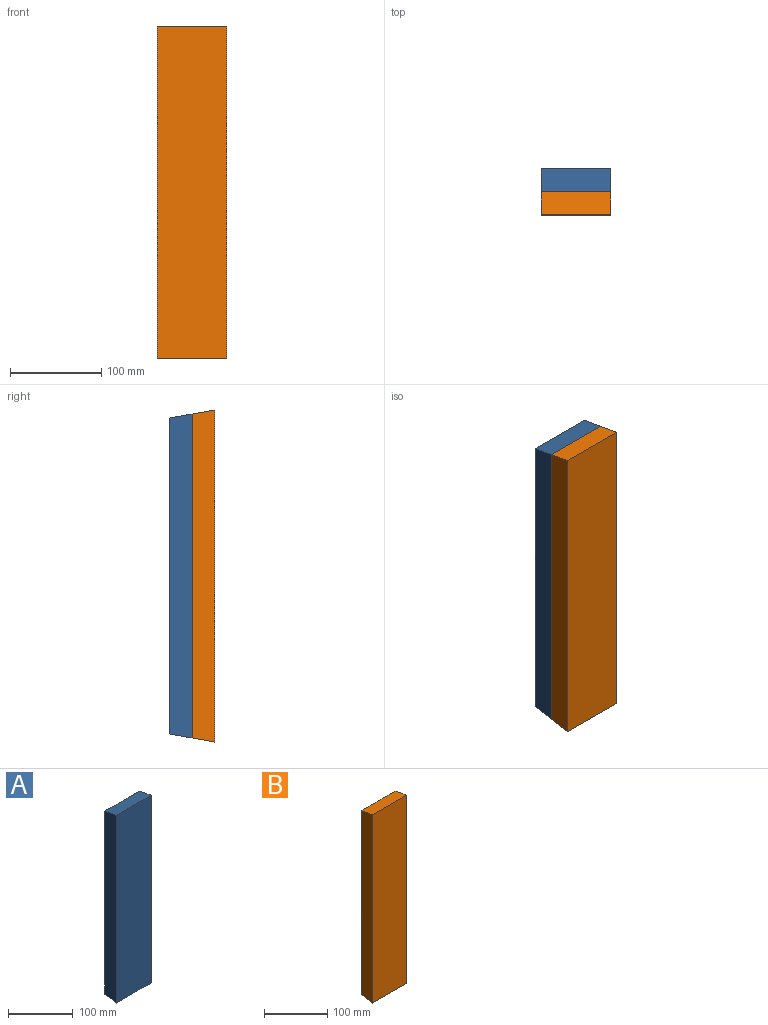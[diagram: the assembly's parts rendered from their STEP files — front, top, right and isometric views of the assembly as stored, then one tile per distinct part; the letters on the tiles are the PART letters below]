
ASSEMBLY  parts=2 mates=1
PART A: 6 faces, bbox 76x25x354.2 mm
  f0: plane 354.2x25mm, normal (1,0,0), area 8744.8mm2, adj f1,f3,f4,f5
  f1: plane 345.38x76mm, normal (0,1,0), area 26249.2mm2, adj f0,f2,f4,f5
  f2: plane 354.2x25mm, normal (-1,0,0), area 8744.8mm2, adj f1,f3,f4,f5
  f3: plane 354.2x76mm, normal (0,-1,0), area 26919.2mm2, adj f0,f2,f4,f5
  f4: plane 76x25mm, normal (0,0.17,-0.98), area 1929.3mm2, adj f0,f1,f2,f3
  f5: plane 76x25mm, normal (0,0.17,0.98), area 1929.3mm2, adj f0,f1,f2,f3
PART B: 6 faces, bbox 76x25x363 mm
  f0: plane 363x25mm, normal (1,0,0), area 8964.8mm2, adj f1,f3,f4,f5
  f1: plane 354.18x76mm, normal (0,1,0), area 26918mm2, adj f0,f2,f4,f5
  f2: plane 363x25mm, normal (-1,0,0), area 8964.8mm2, adj f1,f3,f4,f5
  f3: plane 363x76mm, normal (0,-1,0), area 27588mm2, adj f0,f2,f4,f5
  f4: plane 76x25mm, normal (0,0.17,-0.98), area 1929.3mm2, adj f0,f1,f2,f3
  f5: plane 76x25mm, normal (0,0.17,0.98), area 1929.3mm2, adj f0,f1,f2,f3
PLACE A t=(-428.19,-168.26,446.94)mm
PLACE B t=(-325.55,-193.26,446.95)mm
MATE fastened A.f3 <-> B.f1  axis (0,-1,0) through (-136.58,-193.26,-178.03)mm
